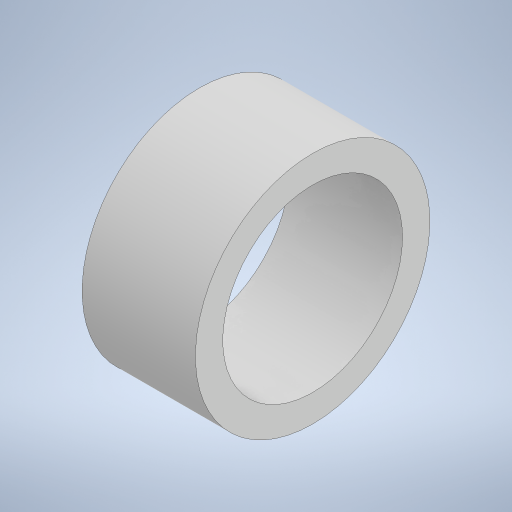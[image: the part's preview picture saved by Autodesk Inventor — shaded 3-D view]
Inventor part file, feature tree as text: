
AUTODESK INVENTOR PART (.ipt)
format: ipt  version: 2023 (Build 270158000, 158)  size: 226,816 bytes
history: native  units: mm
features: extrude x3, sketch x3, other x1
ambient origin geometry x8: Origin, YZ Plane, XZ Plane, XY Plane, X Axis, Y Axis, Z Axis, Center Point
bodies: Body1 (feature_tree)
feature tree (7):
  other  "Bryła1"
  extrude  "Wyciągnięcie proste1"  Depth=30.0mm
  extrude  "Wyciągnięcie proste2"  Depth=3.5mm
  extrude  "Wyciągnięcie proste3"  Depth=14.5mm TaperAngle=0.0deg
  sketch  "Szkic1"
  sketch  "Szkic2"
  sketch  "Szkic3"
